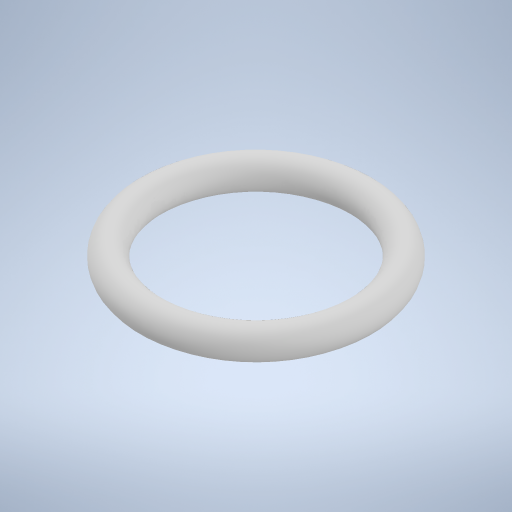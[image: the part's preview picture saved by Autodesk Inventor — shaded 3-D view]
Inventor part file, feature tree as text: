
AUTODESK INVENTOR PART (.ipt)
format: ipt  version: 2023 (Build 270158000, 158)  size: 267,776 bytes
history: native  units: in
note: dims shown in document units (in); Inventor stores cm internally (conversion verified against a paired STEP export)
features: sketch x2, sweep x1
ambient origin geometry x8: Origin, YZ Plane, XZ Plane, XY Plane, X Axis, Y Axis, Z Axis, Center Point
bodies: Body1 (feature_tree)
feature tree (3):
  sweep  "Sweep2"
  sketch  "Sketch3"  dims[d7=1.5in d9=0.0in d10=0.0in]
  sketch  "Sketch4"
